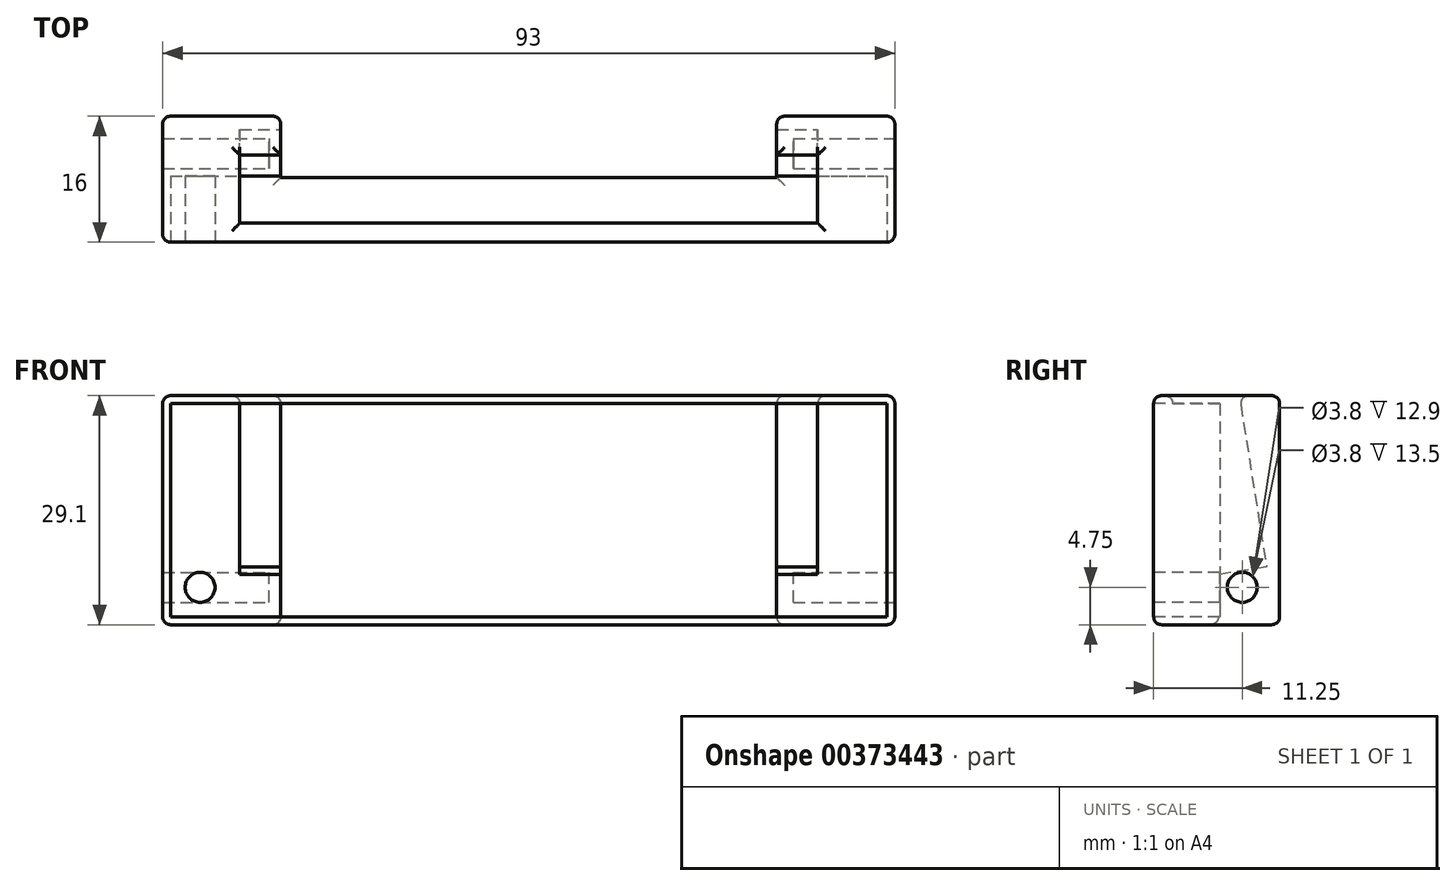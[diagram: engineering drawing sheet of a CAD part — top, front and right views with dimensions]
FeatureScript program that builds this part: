
annotation { "Feature Type Name" : "Feature", "Feature Type Description" : "" }
export const myFeature = defineFeature(function(context is Context, id is Id, definition is map)
    precondition{}
    {
        {
            var Q0;
            Q0=qCreatedBy(makeId("Top.planeOp"),FACE);
            var sketch = newSketch(context, id + "F0", { "sketchPlane" : qUnion([Q0])});
            skLineSegment(sketch, "E0.bottom", {"start": v(-46.5, 0) * mm, "end": v(46.5, 0) * mm});
            skLineSegment(sketch, "E0.top", {"start": v(-46.5, -16) * mm, "end": v(46.5, -16) * mm});
            skLineSegment(sketch, "E0.left", {"start": v(-46.5, 0) * mm, "end": v(-46.5, -16) * mm});
            skLineSegment(sketch, "E0.right", {"start": v(46.5, 0) * mm, "end": v(46.5, -16) * mm});
            skLineSegment(sketch, "E1.bottom", {"start": v(-31.5, 17.54) * mm, "end": v(31.5, 17.54) * mm});
            skLineSegment(sketch, "E1.top", {"start": v(-31.5, -7.78) * mm, "end": v(31.5, -7.78) * mm});
            skLineSegment(sketch, "E1.left", {"start": v(-31.5, 17.54) * mm, "end": v(-31.5, -7.78) * mm});
            skLineSegment(sketch, "E1.right", {"start": v(31.5, 17.54) * mm, "end": v(31.5, -7.78) * mm});
            skSolve(sketch);
        }
        {
            var Q0;
            Q0=makeQuery(id+"F0.imprint","IMPRINT",FACE,{"disambiguationData":[TD([[makeQuery(id+"F0.imprint","IMPRINT",EDGE,{"derivedFrom":sQuery(id+"F0.wireOp",EDGE,"E0.bottom")}),-1.0]])]});
            var Q1;
            {var subQ5=sQuery(id+"F0.wireOp",EDGE,"E1.top");Q1=makeQuery(id+"F0.imprint","IMPRINT",FACE,{"disambiguationData":[TD([[makeQuery(id+"F0.imprint","IMPRINT",EDGE,{"derivedFrom":subQ5}),1.0]])]});}
            extrude(context, id + "F1", {"entities" : qUnion([Q0, Q1]), "depth" : 29.1 * mm});
        }
        {
            var Q0;
            Q0=sQuery(id+"F0.wireOp",EDGE,"E0.top");
            cPlane(context, id + "F2", {"entities" : qUnion([Q0]), "cplaneType" : CPlaneType.LINE_ANGLE, "offset" : 25 * mm, "angle" : 99 * degree, "width" : 150 * mm, "height" : 150 * mm});
        }
        {
            var Q0;
            Q0=qCreatedBy(id+"F2.planeOp",FACE);
            var sketch = newSketch(context, id + "F3", { "sketchPlane" : qUnion([Q0])});
            skLineSegment(sketch, "E2.bottom", {"start": v(-36.7, -0.5) * mm, "end": v(36.7, -0.5) * mm});
            skLineSegment(sketch, "E2.top", {"start": v(-36.7, -9) * mm, "end": v(36.7, -9) * mm});
            skLineSegment(sketch, "E2.left", {"start": v(-36.7, -0.5) * mm, "end": v(-36.7, -9) * mm});
            skLineSegment(sketch, "E2.right", {"start": v(36.7, -0.5) * mm, "end": v(36.7, -9) * mm});
            skSolve(sketch);
        }
        {
            var Q0;
            Q0 = qSketchRegion(id + "F3", true);
            extrude(context, id + "F4", {"entities" : qUnion([Q0]), "operationType" : NewBodyOperationType.REMOVE, "depth" : 39.9 * mm, "hasSecondDirection" : true, "secondDirectionOppositeDirection" : false, "secondDirectionDepth" : 5 * mm});
        }
        {
            var Q0;
            {var subQ5=sQuery(id+"F0.wireOp",EDGE,"E1.bottom");Q0=makeQuery(id+"F0.imprint","IMPRINT",FACE,{"disambiguationData":[TD([[makeQuery(id+"F0.imprint","IMPRINT",EDGE,{"derivedFrom":subQ5}),-1.0]])]});}
            var Q1;
            {var subQ5=sQuery(id+"F0.wireOp",EDGE,"E1.top");Q1=makeQuery(id+"F0.imprint","IMPRINT",FACE,{"disambiguationData":[TD([[makeQuery(id+"F0.imprint","IMPRINT",EDGE,{"derivedFrom":subQ5}),1.0]])]});}
            extrude(context, id + "F5", {"entities" : qUnion([Q0, Q1]), "operationType" : NewBodyOperationType.REMOVE, "depth" : 44.7 * mm});
        }
        {
            var Q0;
            Q0=makeQuery(id+"F1.opExtrude","CAP_FACE",FACE,{"disambiguationData":[OSD([sQuery(id+"F0.wireOp",EDGE,"E0.bottom"),sQuery(id+"F0.wireOp",EDGE,"E0.top"),sQuery(id+"F0.wireOp",EDGE,"E0.left"),sQuery(id+"F0.wireOp",EDGE,"E0.right")])],"isStart":false});
            var Q1;
            Q1=makeQuery(id+"F1.opExtrude","SWEPT_FACE",FACE,{"disambiguationData":[OSD([sQuery(id+"F0.wireOp",EDGE,"E0.left")])]});
            var Q2;
            Q2=makeQuery(id+"F1.opExtrude","SWEPT_FACE",FACE,{"disambiguationData":[OSD([sQuery(id+"F0.wireOp",EDGE,"E0.top")])]});
            var Q3;
            Q3=makeQuery(id+"F1.opExtrude","SWEPT_FACE",FACE,{"disambiguationData":[OSD([sQuery(id+"F0.wireOp",EDGE,"E0.right")])]});
            var Q4;
            {var subQ0=sQuery(id+"F0.wireOp",EDGE,"E0.right");var subQ3=sQuery(id+"F0.wireOp",EDGE,"E0.bottom");Q4=makeQuery(id+"F5.boolean.opBoolean","SPLIT",FACE,{"disambiguationData":[TD([makeQuery(id+"F1.opExtrude","SWEPT_FACE",FACE,{"disambiguationData":[OSD([subQ0])]})])],"derivedFrom":makeQuery(id+"F1.opExtrude","SWEPT_FACE",FACE,{"disambiguationData":[OSD([subQ3])]})});}
            var Q5;
            Q5=makeQuery(id+"F5.boolean.opBoolean","INTERSECT",EDGE,{"derivedFrom":[makeQuery(id+"F1.opExtrude","SWEPT_FACE",FACE,{"disambiguationData":[OSD([sQuery(id+"F0.wireOp",EDGE,"E0.bottom")])]}),makeQuery(id+"F5.opExtrude","SWEPT_FACE",FACE,{"disambiguationData":[OSD([sQuery(id+"F0.wireOp",EDGE,"E1.left")])]})]});
            var Q6;
            Q6=makeQuery(id+"F1.opExtrude","CAP_FACE",FACE,{"disambiguationData":[OSD([sQuery(id+"F0.wireOp",EDGE,"E0.bottom"),sQuery(id+"F0.wireOp",EDGE,"E0.top"),sQuery(id+"F0.wireOp",EDGE,"E0.left"),sQuery(id+"F0.wireOp",EDGE,"E0.right")])],"isStart":true});
            fillet(context, id + "F6", {"entities" : qUnion([Q0, Q1, Q2, Q3, Q4, Q5, Q6]), "radius" : 1 * mm, "tangentPropagation" : true, "allowEdgeOverflow" : false});
        }
        {
            var Q0;
            Q0=makeQuery(id+"F1.opExtrude","SWEPT_FACE",FACE,{"disambiguationData":[OSD([sQuery(id+"F0.wireOp",EDGE,"E0.right")])]});
            var sketch = newSketch(context, id + "F7", { "sketchPlane" : qUnion([Q0])});
            skCircle(sketch, "E3", {"center": v(-4.75, 4.75) * mm, "radius": 1.9 * mm});
            skSolve(sketch);
        }
        {
            var Q0;
            Q0=makeQuery(id+"F7.imprint","IMPRINT",FACE,{"disambiguationData":[TD([[makeQuery(id+"F7.imprint","IMPRINT",EDGE,{"derivedFrom":sQuery(id+"F7.wireOp",EDGE,"E3")}),1.0]])]});
            extrude(context, id + "F8", {"entities" : qUnion([Q0]), "operationType" : NewBodyOperationType.REMOVE, "oppositeDirection" : true, "depth" : 12.9 * mm});
        }
        {
            var Q0;
            Q0=makeQuery(id+"F1.opExtrude","SWEPT_FACE",FACE,{"disambiguationData":[OSD([sQuery(id+"F0.wireOp",EDGE,"E0.top")])]});
            var sketch = newSketch(context, id + "F9", { "sketchPlane" : qUnion([Q0])});
            skCircle(sketch, "E4", {"center": v(41.75, 4.75) * mm, "radius": 1.9 * mm});
            skCircle(sketch, "E5.MirrorC", {"center": v(-41.75, 4.75) * mm, "radius": 1.9 * mm});
            skSolve(sketch);
        }
        {
            var Q0;
            Q0=makeQuery(id+"F9.imprint","IMPRINT",FACE,{"disambiguationData":[TD([[makeQuery(id+"F9.imprint","IMPRINT",EDGE,{"derivedFrom":sQuery(id+"F9.wireOp",EDGE,"E4")}),1.0]])]});
            var Q1;
            Q1=makeQuery(id+"F9.imprint","IMPRINT",FACE,{"disambiguationData":[TD([[makeQuery(id+"F9.imprint","IMPRINT",EDGE,{"derivedFrom":sQuery(id+"F9.wireOp",EDGE,"E5.MirrorC")}),-1.0]])]});
            extrude(context, id + "F10", {"entities" : qUnion([Q0, Q1]), "operationType" : NewBodyOperationType.REMOVE, "oppositeDirection" : true, "depth" : 8.4 * mm});
        }
        {
            var Q0;
            Q0=makeQuery(id+"F7.imprint","IMPRINT",FACE,{"disambiguationData":[TD([[makeQuery(id+"F7.imprint","IMPRINT",EDGE,{"derivedFrom":sQuery(id+"F7.wireOp",EDGE,"E3")}),1.0]])]});
            extrude(context, id + "F11", {"entities" : qUnion([Q0]), "operationType" : NewBodyOperationType.REMOVE, "oppositeDirection" : true, "depth" : 114.8 * mm, "hasSecondDirection" : true, "secondDirectionOppositeDirection" : true, "secondDirectionDepth" : 79.5 * mm});
        }
    });
